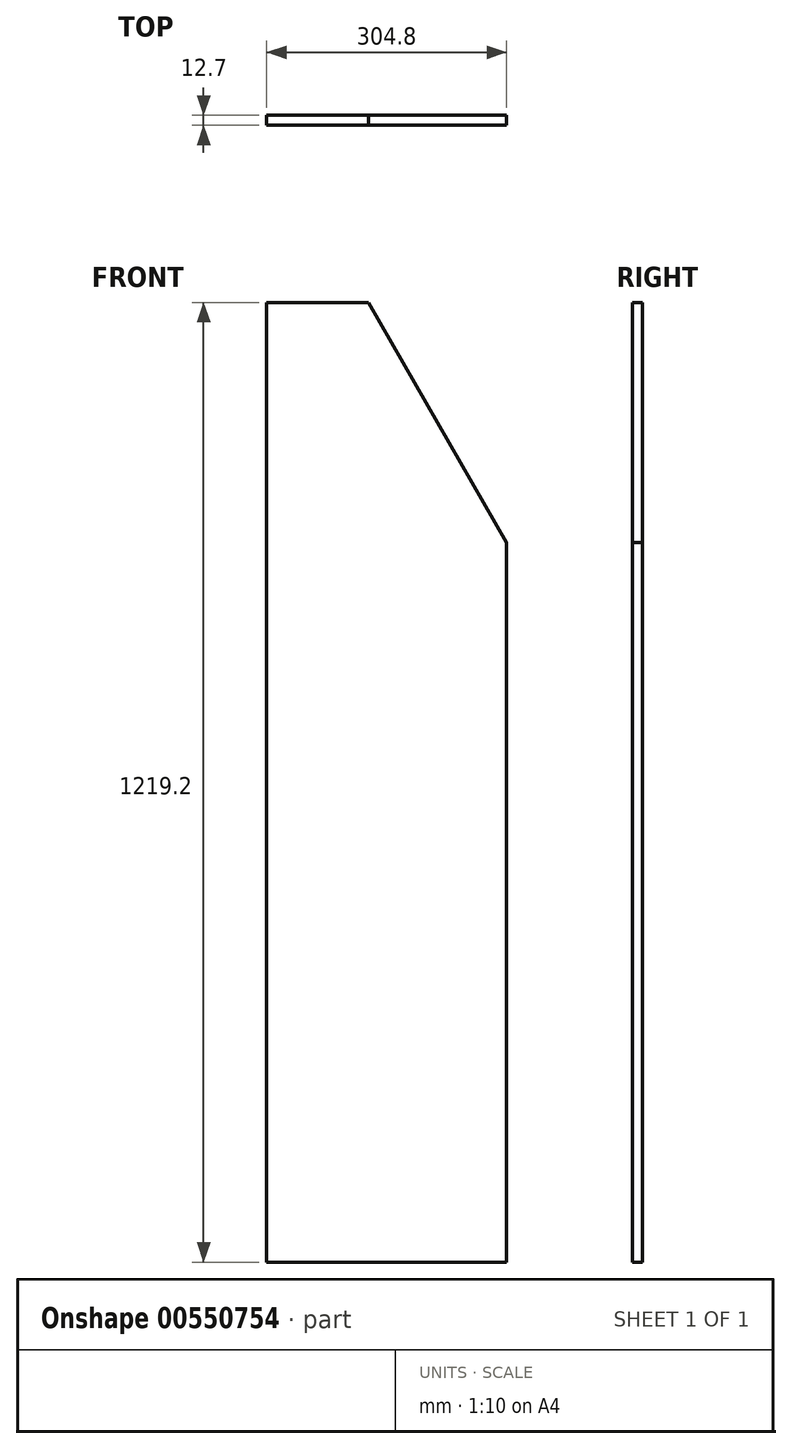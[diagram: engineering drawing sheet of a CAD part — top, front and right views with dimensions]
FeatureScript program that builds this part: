
annotation { "Feature Type Name" : "Feature", "Feature Type Description" : "" }
export const myFeature = defineFeature(function(context is Context, id is Id, definition is map)
    precondition{}
    {
        {
            var Q0;
            Q0=qCreatedBy(makeId("Front.planeOp"),FACE);
            var sketch = newSketch(context, id + "F0", { "sketchPlane" : qUnion([Q0])});
            skLineSegment(sketch, "E0", {"start": v(0, 0) * mm, "end": v(0, 1219.2) * mm});
            skLineSegment(sketch, "E1", {"start": v(304.8, 914.4) * mm, "end": v(304.8, 0) * mm});
            skLineSegment(sketch, "E2", {"start": v(304.8, 0) * mm, "end": v(0, 0) * mm});
            skLineSegment(sketch, "E3", {"start": v(0, 1219.2) * mm, "end": v(129.33, 1219.2) * mm});
            skLineSegment(sketch, "E4", {"start": v(129.33, 1219.2) * mm, "end": v(304.8, 914.4) * mm});
            skSolve(sketch);
        }
        {
            var Q0;
            Q0=makeQuery(id+"F0.imprint","IMPRINT",FACE,{"disambiguationData":[TD([[makeQuery(id+"F0.imprint","IMPRINT",EDGE,{"derivedFrom":sQuery(id+"F0.wireOp",EDGE,"E0")}),-1.0]])]});
            extrude(context, id + "F1", {"entities" : qUnion([Q0]), "oppositeDirection" : true, "depth" : 12.7 * mm, "offsetDistance" : 25.4 * mm});
        }
    });
